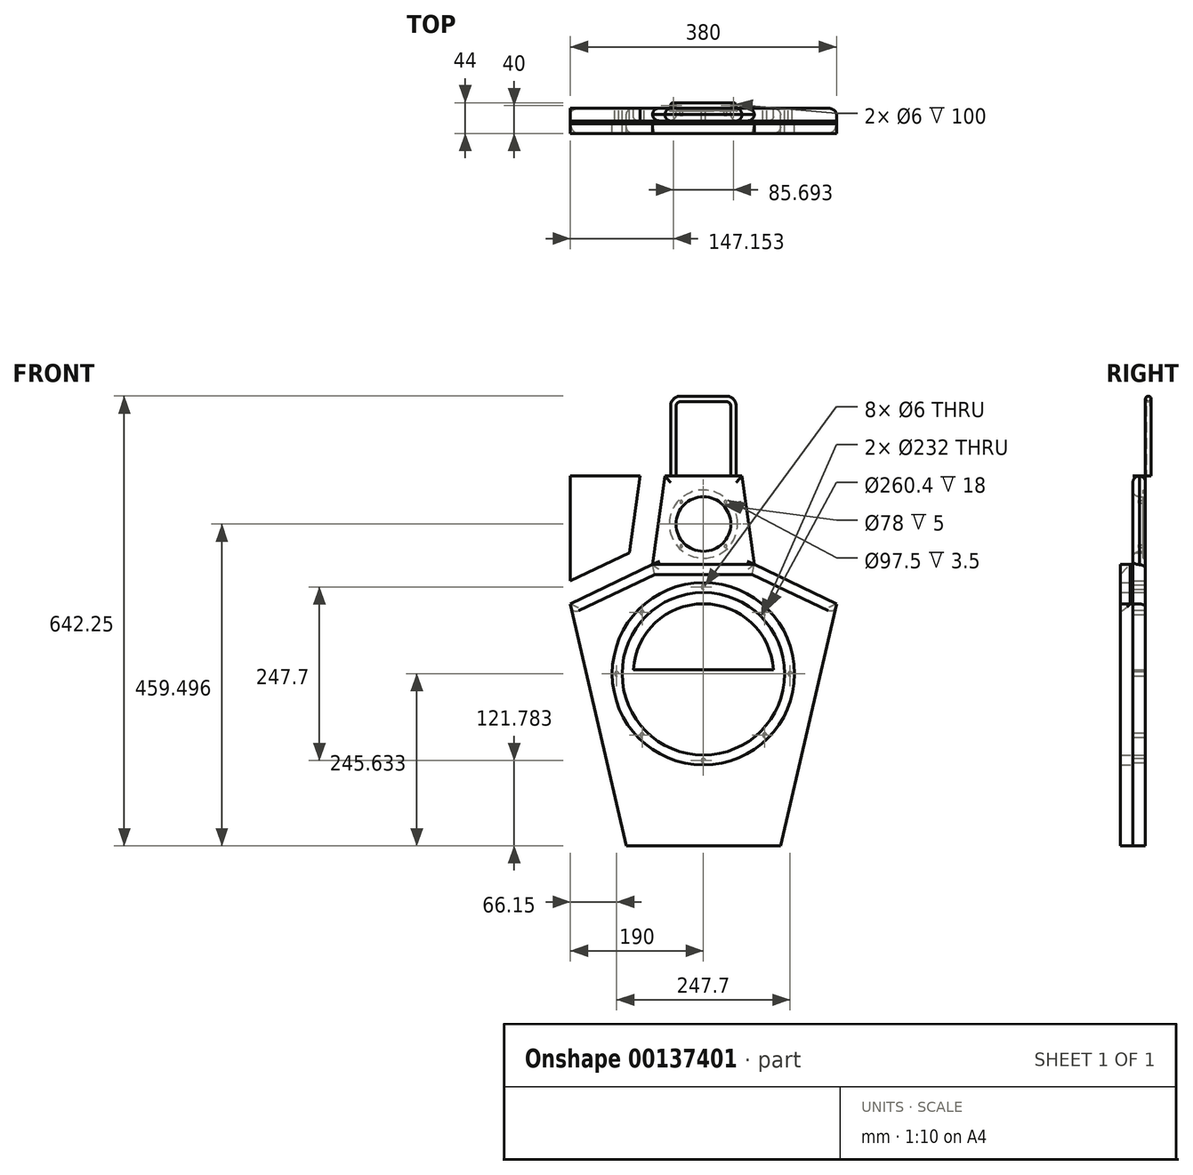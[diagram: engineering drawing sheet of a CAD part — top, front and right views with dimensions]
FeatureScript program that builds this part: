
annotation { "Feature Type Name" : "Feature", "Feature Type Description" : "" }
export const myFeature = defineFeature(function(context is Context, id is Id, definition is map)
    precondition{}
    {
        {
            var Q0;
            Q0=qCreatedBy(makeId("Front.planeOp"),FACE);
            var sketch = newSketch(context, id + "F0", { "sketchPlane" : qUnion([Q0])});
            skCircle(sketch, "E0", {"center": v(0, 113.89) * mm, "radius": 39 * mm});
            skCircle(sketch, "E1", {"center": v(0, -99.98) * mm, "radius": 116 * mm});
            skCircle(sketch, "E2", {"center": v(0, 113.89) * mm, "radius": 48.75 * mm, "construction": true});
            skCircle(sketch, "E3", {"center": v(0, -99.98) * mm, "radius": 130.2 * mm, "construction": true});
            skLineSegment(sketch, "E4", {"start": v(0, 270.1) * mm, "end": v(0, -456.04) * mm, "construction": true});
            skLineSegment(sketch, "E5", {"start": v(0, 182.64) * mm, "end": v(-55, 182.64) * mm});
            skCircle(sketch, "E6", {"center": v(0, -99.98) * mm, "radius": 146 * mm, "construction": true});
            skCircle(sketch, "E7", {"center": v(0, 113.89) * mm, "radius": 64 * mm, "construction": true});
            skLineSegment(sketch, "E8", {"start": v(-55, 182.64) * mm, "end": v(-72.73, 55.98) * mm});
            skLineSegment(sketch, "E9", {"start": v(0, -345.6) * mm, "end": v(-110, -345.6) * mm});
            skLineSegment(sketch, "E10", {"start": v(-110, -345.6) * mm, "end": v(-190, 0) * mm});
            skLineSegment(sketch, "E11", {"start": v(-72.73, 55.98) * mm, "end": v(-190, 0) * mm});
            skLineSegment(sketch, "E12.MirrorCS", {"start": v(0, 182.64) * mm, "end": v(55, 182.64) * mm});
            skLineSegment(sketch, "E13.MirrorCS", {"start": v(55, 182.64) * mm, "end": v(72.73, 55.98) * mm});
            skLineSegment(sketch, "E14.MirrorCS", {"start": v(72.73, 55.98) * mm, "end": v(190, 0) * mm});
            skLineSegment(sketch, "E15.MirrorCS", {"start": v(110, -345.6) * mm, "end": v(190, 0) * mm});
            skLineSegment(sketch, "E16.MirrorCS", {"start": v(0, -345.6) * mm, "end": v(110, -345.6) * mm});
            skLineSegment(sketch, "E17.bottom", {"start": v(-110, -195.6) * mm, "end": v(-92, -195.6) * mm, "construction": true});
            skLineSegment(sketch, "E17.top", {"start": v(-110, -345.6) * mm, "end": v(-92, -345.6) * mm});
            skLineSegment(sketch, "E17.left", {"start": v(-110, -195.6) * mm, "end": v(-110, -345.6) * mm, "construction": true});
            skLineSegment(sketch, "E17.right", {"start": v(-92, -195.6) * mm, "end": v(-92, -345.6) * mm, "construction": true});
            skLineSegment(sketch, "E18.MirrorCS", {"start": v(92, -195.6) * mm, "end": v(92, -345.6) * mm, "construction": true});
            skLineSegment(sketch, "E19.MirrorCS", {"start": v(110, -195.6) * mm, "end": v(92, -195.6) * mm, "construction": true});
            skLineSegment(sketch, "E20.MirrorCS", {"start": v(110, -195.6) * mm, "end": v(110, -345.6) * mm, "construction": true});
            skLineSegment(sketch, "E21.MirrorCS", {"start": v(110, -345.6) * mm, "end": v(92, -345.6) * mm, "construction": true});
            skLineSegment(sketch, "E22", {"start": v(-140.08, -245.59) * mm, "end": v(-90.27, -193.8) * mm, "construction": true});
            skLineSegment(sketch, "E23", {"start": v(-72.73, 55.98) * mm, "end": v(72.73, 55.98) * mm});
            skLineSegment(sketch, "E24", {"start": v(-92, -327.6) * mm, "end": v(92, -327.6) * mm, "construction": true});
            skLineSegment(sketch, "E25", {"start": v(-190, 182.64) * mm, "end": v(-90.37, 182.64) * mm});
            skLineSegment(sketch, "E26", {"start": v(-90.37, 182.64) * mm, "end": v(-105.74, 72.86) * mm});
            skLineSegment(sketch, "E27", {"start": v(-190, 32.64) * mm, "end": v(-105.74, 72.86) * mm});
            skLineSegment(sketch, "E28", {"start": v(-190, 32.64) * mm, "end": v(-190, 182.64) * mm});
            skLineSegment(sketch, "E29", {"start": v(-190, 0) * mm, "end": v(-190, 32.64) * mm, "construction": true});
            skLineSegment(sketch, "E30", {"start": v(-90.37, 182.64) * mm, "end": v(-55, 182.64) * mm, "construction": true});
            skCircle(sketch, "E31", {"center": v(0, -99.98) * mm, "radius": 100 * mm, "construction": true});
            skLineSegment(sketch, "E32", {"start": v(-99.82, -93.98) * mm, "end": v(99.82, -93.98) * mm});
            skLineSegment(sketch, "E33", {"start": v(-99.82, -105.98) * mm, "end": v(99.82, -105.98) * mm, "construction": true});
            skLineSegment(sketch, "E34", {"start": v(-100, -99.98) * mm, "end": v(100, -99.98) * mm, "construction": true});
            skArc(sketch, "E35", {"start": v(-99.82, -93.98) * mm, "mid": v(0, 0.02) * mm, "end": v(99.82, -93.98) * mm});
            skLineSegment(sketch, "E36", {"start": v(0, -345.6) * mm, "end": v(0, -245.98) * mm, "construction": true});
            skCircle(sketch, "E37", {"center": v(0, 113.89) * mm, "radius": 44.75 * mm, "construction": true});
            skLineSegment(sketch, "E38", {"start": v(-84.86, 113.89) * mm, "end": v(97.18, 113.89) * mm, "construction": true});
            skSolve(sketch);
        }
        {
            var Q0;
            Q0=makeQuery(id+"F0.imprint","IMPRINT",FACE,{"disambiguationData":[TD([[makeQuery(id+"F0.imprint","IMPRINT",EDGE,{"derivedFrom":sQuery(id+"F0.wireOp",EDGE,"E0")}),-1.0]])]});
            var Q1;
            Q1=makeQuery(id+"F0.imprint","IMPRINT",FACE,{"disambiguationData":[TD([[makeQuery(id+"F0.imprint","IMPRINT",EDGE,{"derivedFrom":sQuery(id+"F0.wireOp",EDGE,"E1")}),-1.0]])]});
            var Q2;
            Q2=makeQuery(id+"F0.imprint","IMPRINT",FACE,{"disambiguationData":[TD([[makeQuery(id+"F0.imprint","IMPRINT",EDGE,{"derivedFrom":sQuery(id+"F0.wireOp",EDGE,"ec5cafb6-0821-4271-814e-014075e78ac90.MirrorCS")}),1.0]])]});
            var Q3;
            Q3=makeQuery(id+"F0.imprint","IMPRINT",FACE,{"disambiguationData":[TD([[makeQuery(id+"F0.imprint","IMPRINT",EDGE,{"derivedFrom":sQuery(id+"F0.wireOp",EDGE,"eULuaSkG-qzq6-M7m6-OuyN-eB9Shyhv74vP")}),-1.0]])]});
            var Q4;
            Q4=makeQuery(id+"F0.imprint","IMPRINT",FACE,{"disambiguationData":[TD([[makeQuery(id+"F0.imprint","IMPRINT",EDGE,{"derivedFrom":sQuery(id+"F0.wireOp",EDGE,"wTw06wgs-Vm1q-qTd6-eUog-KbhtCCmFDIgU")}),1.0]])]});
            var Q5;
            Q5=makeQuery(id+"F0.imprint","IMPRINT",FACE,{"disambiguationData":[TD([[makeQuery(id+"F0.imprint","IMPRINT",EDGE,{"derivedFrom":sQuery(id+"F0.wireOp",EDGE,"97328e8b-8490-4f0b-808f-8670b9d821d80.MirrorC")}),-1.0]])]});
            var Q6;
            {var subQ0=sQuery(id+"F0.wireOp",EDGE,"54e6497e-5cba-44bf-835f-aaa9bed86e8d0.MirrorC");var subQ1=sQuery(id+"F0.wireOp",EDGE,"67c14ce4-3d45-40ac-80a8-5606c36c91ac.0");var subQ2=makeQuery(id+"F0.imprint","INTERSECT",VERTEX,{"disambiguationData":[OD(0.0)],"derivedFrom":[subQ1,subQ0]});Q6=makeQuery(id+"F0.imprint","IMPRINT",FACE,{"disambiguationData":[TD([[makeQuery(id+"F0.imprint","IMPRINT",EDGE,{"disambiguationData":[TD([[subQ2,-1.0]])],"derivedFrom":subQ1}),1.0]])]});}
            var Q7;
            {var subQ0=sQuery(id+"F0.wireOp",EDGE,"SJXep4Ca-SblW-kjJo-KBgL-TVq6fpib3Pzp");var subQ1=sQuery(id+"F0.wireOp",EDGE,"3cbaf5a3-71d0-46ca-a7cf-13315173ab510.MirrorCS");var subQ2=makeQuery(id+"F0.imprint","INTERSECT",VERTEX,{"disambiguationData":[OD(0.0)],"derivedFrom":[subQ1,subQ0]});Q7=makeQuery(id+"F0.imprint","IMPRINT",FACE,{"disambiguationData":[TD([[makeQuery(id+"F0.imprint","IMPRINT",EDGE,{"disambiguationData":[TD([[subQ2,-1.0]])],"derivedFrom":subQ1}),-1.0]])]});}
            extrude(context, id + "F1", {"entities" : qUnion([Q0, Q1, Q2, Q3, Q4, Q5, Q6, Q7]), "depth" : 18 * mm});
        }
        {
            var Q0;
            Q0=makeQuery(id+"F0.imprint","IMPRINT",FACE,{"disambiguationData":[TD([[makeQuery(id+"F0.imprint","IMPRINT",EDGE,{"derivedFrom":sQuery(id+"F0.wireOp",EDGE,"E1")}),-1.0]])]});
            var Q1;
            Q1=makeQuery(id+"F0.imprint","IMPRINT",FACE,{"disambiguationData":[TD([[makeQuery(id+"F0.imprint","IMPRINT",EDGE,{"derivedFrom":sQuery(id+"F0.wireOp",EDGE,"eULuaSkG-qzq6-M7m6-OuyN-eB9Shyhv74vP")}),-1.0]])]});
            var Q2;
            Q2=makeQuery(id+"F0.imprint","IMPRINT",FACE,{"disambiguationData":[TD([[makeQuery(id+"F0.imprint","IMPRINT",EDGE,{"derivedFrom":sQuery(id+"F0.wireOp",EDGE,"ec5cafb6-0821-4271-814e-014075e78ac90.MirrorCS")}),1.0]])]});
            var Q3;
            Q3=makeQuery(id+"F0.imprint","IMPRINT",FACE,{"disambiguationData":[TD([[makeQuery(id+"F0.imprint","IMPRINT",EDGE,{"derivedFrom":sQuery(id+"F0.wireOp",EDGE,"wTw06wgs-Vm1q-qTd6-eUog-KbhtCCmFDIgU")}),1.0]])]});
            var Q4;
            Q4=makeQuery(id+"F0.imprint","IMPRINT",FACE,{"disambiguationData":[TD([[makeQuery(id+"F0.imprint","IMPRINT",EDGE,{"derivedFrom":sQuery(id+"F0.wireOp",EDGE,"97328e8b-8490-4f0b-808f-8670b9d821d80.MirrorC")}),-1.0]])]});
            var Q5;
            {var subQ0=sQuery(id+"F0.wireOp",EDGE,"SJXep4Ca-SblW-kjJo-KBgL-TVq6fpib3Pzp");var subQ1=sQuery(id+"F0.wireOp",EDGE,"3cbaf5a3-71d0-46ca-a7cf-13315173ab510.MirrorCS");var subQ2=makeQuery(id+"F0.imprint","INTERSECT",VERTEX,{"disambiguationData":[OD(0.0)],"derivedFrom":[subQ1,subQ0]});Q5=makeQuery(id+"F0.imprint","IMPRINT",FACE,{"disambiguationData":[TD([[makeQuery(id+"F0.imprint","IMPRINT",EDGE,{"disambiguationData":[TD([[subQ2,-1.0]])],"derivedFrom":subQ1}),-1.0]])]});}
            var Q6;
            {var subQ0=sQuery(id+"F0.wireOp",EDGE,"54e6497e-5cba-44bf-835f-aaa9bed86e8d0.MirrorC");var subQ1=sQuery(id+"F0.wireOp",EDGE,"67c14ce4-3d45-40ac-80a8-5606c36c91ac.0");var subQ2=makeQuery(id+"F0.imprint","INTERSECT",VERTEX,{"disambiguationData":[OD(0.0)],"derivedFrom":[subQ1,subQ0]});Q6=makeQuery(id+"F0.imprint","IMPRINT",FACE,{"disambiguationData":[TD([[makeQuery(id+"F0.imprint","IMPRINT",EDGE,{"disambiguationData":[TD([[subQ2,-1.0]])],"derivedFrom":subQ1}),1.0]])]});}
            extrude(context, id + "F2", {"entities" : qUnion([Q0, Q1, Q2, Q3, Q4, Q5, Q6]), "depth" : 18 * mm});
        }
        {
            var Q0;
            Q0=makeQuery(id+"F2.opExtrude","SWEPT_BODY",BODY,{"disambiguationData":[OSD([sQuery(id+"F0.wireOp",EDGE,"E1"),sQuery(id+"F0.wireOp",EDGE,"E9"),sQuery(id+"F0.wireOp",EDGE,"E10"),sQuery(id+"F0.wireOp",EDGE,"E11"),sQuery(id+"F0.wireOp",EDGE,"E14.MirrorCS"),sQuery(id+"F0.wireOp",EDGE,"E15.MirrorCS"),sQuery(id+"F0.wireOp",EDGE,"E16.MirrorCS"),sQuery(id+"F0.wireOp",EDGE,"E17.top"),sQuery(id+"F0.wireOp",EDGE,"E23")])]});
            var Q1;
            Q1=makeQuery(id+"F2.opExtrude","SWEPT_EDGE",EDGE,{"disambiguationData":[OSD([sQuery(id+"F0.wireOp",EDGE,"E14.MirrorCS"),sQuery(id+"F0.wireOp",EDGE,"E15.MirrorCS")])]});
            transform(context, id + "F3", {"entities" : qUnion([Q0]), "transformType" : TransformType.TRANSLATION_DISTANCE, "transformDirection" : qUnion([Q1]), "distance" : 18 * mm, "oppositeDirection" : true, "makeCopy" : false});
        }
        {
            var Q0;
            Q0=makeQuery(id+"F0.imprint","IMPRINT",FACE,{"disambiguationData":[TD([[makeQuery(id+"F0.imprint","IMPRINT",EDGE,{"derivedFrom":sQuery(id+"F0.wireOp",EDGE,"E32")}),1.0]])]});
            extrude(context, id + "F4", {"entities" : qUnion([Q0]), "depth" : 18 * mm});
        }
        {
            var Q0;
            Q0=makeQuery(id+"F0.imprint","IMPRINT",FACE,{"disambiguationData":[TD([[makeQuery(id+"F0.imprint","IMPRINT",EDGE,{"derivedFrom":sQuery(id+"F0.wireOp",EDGE,"E25")}),-1.0]])]});
            extrude(context, id + "F5", {"entities" : qUnion([Q0]), "depth" : 18 * mm});
        }
        {
            var Q0;
            Q0=makeQuery(id+"F1.opExtrude","SWEPT_FACE",FACE,{"disambiguationData":[OSD([sQuery(id+"F0.wireOp",EDGE,"E5"),sQuery(id+"F0.wireOp",EDGE,"E12.MirrorCS")])]});
            var sketch = newSketch(context, id + "F6", { "sketchPlane" : qUnion([Q0])});
            skLineSegment(sketch, "E39", {"start": v(-42.85, 4) * mm, "end": v(42.85, 4) * mm, "construction": true});
            skLineSegment(sketch, "E40", {"start": v(0, 0) * mm, "end": v(0, -18) * mm, "construction": true});
            skCircle(sketch, "E41", {"center": v(-42.85, 4) * mm, "radius": 4 * mm});
            skCircle(sketch, "E42", {"center": v(-42.85, 4) * mm, "radius": 3 * mm});
            skCircle(sketch, "E43.MirrorC", {"center": v(42.85, 4) * mm, "radius": 3 * mm});
            skCircle(sketch, "E44.MirrorC", {"center": v(42.85, 4) * mm, "radius": 4 * mm});
            skSolve(sketch);
        }
        {
            var Q0;
            Q0=qCreatedBy(makeId("Front.planeOp"),FACE);
            cPlane(context, id + "F7", {"entities" : qUnion([Q0]), "cplaneType" : CPlaneType.OFFSET, "offset" : 4 * mm, "oppositeDirection" : true, "width" : 150 * mm, "height" : 150 * mm});
        }
        {
            var Q0;
            Q0=qCreatedBy(id+"F7.planeOp",FACE);
            var sketch = newSketch(context, id + "F8", { "sketchPlane" : qUnion([Q0])});
            skLineSegment(sketch, "E45", {"start": v(0, 225.34) * mm, "end": v(0, 315.34) * mm, "construction": true});
            skLineSegment(sketch, "E46", {"start": v(42.85, 182.64) * mm, "end": v(42.85, 282.64) * mm});
            skLineSegment(sketch, "E47", {"start": v(32.85, 292.64) * mm, "end": v(-32.85, 292.64) * mm});
            skLineSegment(sketch, "E48", {"start": v(-42.85, 282.64) * mm, "end": v(-42.85, 182.64) * mm});
            skPoint(sketch, "E49.visualSharp", {"position": v(-42.85, 292.64) * mm});
            skArc(sketch, "E49.filletArc", {"start": v(-32.85, 292.64) * mm, "mid": v(-39.92, 289.7) * mm, "end": v(-42.85, 282.64) * mm});
            skPoint(sketch, "E50.visualSharp", {"position": v(42.85, 292.64) * mm});
            skArc(sketch, "E50.filletArc", {"start": v(42.85, 282.64) * mm, "mid": v(39.92, 289.7) * mm, "end": v(32.85, 292.64) * mm});
            skSolve(sketch);
        }
        {
            var Q0;
            Q0=makeQuery(id+"F6.imprint","IMPRINT",FACE,{"disambiguationData":[TD([[makeQuery(id+"F6.imprint","IMPRINT",EDGE,{"derivedFrom":sQuery(id+"F6.wireOp",EDGE,"E41")}),1.0]])]});
            var Q1;
            Q1=sQuery(id+"F8.wireOp",EDGE,"E48");
            var Q2;
            Q2=sQuery(id+"F8.wireOp",EDGE,"E49.filletArc");
            var Q3;
            Q3=sQuery(id+"F8.wireOp",EDGE,"E47");
            var Q4;
            Q4=sQuery(id+"F8.wireOp",EDGE,"E50.filletArc");
            var Q5;
            Q5=sQuery(id+"F8.wireOp",EDGE,"E46");
            sweep(context, id + "F9", {"profiles" : qUnion([Q0]), "path" : qUnion([Q1, Q2, Q3, Q4, Q5])});
        }
        {
            var Q0;
            Q0=makeQuery(id+"F1.opExtrude","CAP_FACE",FACE,{"disambiguationData":[OSD([sQuery(id+"F0.wireOp",EDGE,"E0"),sQuery(id+"F0.wireOp",EDGE,"E1"),sQuery(id+"F0.wireOp",EDGE,"E5"),sQuery(id+"F0.wireOp",EDGE,"E8"),sQuery(id+"F0.wireOp",EDGE,"E9"),sQuery(id+"F0.wireOp",EDGE,"E10"),sQuery(id+"F0.wireOp",EDGE,"E11"),sQuery(id+"F0.wireOp",EDGE,"E12.MirrorCS"),sQuery(id+"F0.wireOp",EDGE,"E13.MirrorCS"),sQuery(id+"F0.wireOp",EDGE,"E14.MirrorCS"),sQuery(id+"F0.wireOp",EDGE,"E15.MirrorCS"),sQuery(id+"F0.wireOp",EDGE,"E16.MirrorCS"),sQuery(id+"F0.wireOp",EDGE,"E17.top")])],"isStart":false});
            var sketch = newSketch(context, id + "F10", { "sketchPlane" : qUnion([Q0])});
            skLineSegment(sketch, "E51.0", {"start": v(72.73, 55.98) * mm, "end": v(190, 0) * mm});
            skLineSegment(sketch, "E52.0", {"start": v(-72.73, 55.98) * mm, "end": v(72.73, 55.98) * mm});
            skLineSegment(sketch, "E53.0", {"start": v(-72.73, 55.98) * mm, "end": v(-190, 0) * mm});
            skLineSegment(sketch, "E54.0", {"start": v(110, -345.6) * mm, "end": v(190, 0) * mm});
            skLineSegment(sketch, "E55.0", {"start": v(-110, -345.6) * mm, "end": v(-190, 0) * mm});
            skLineSegment(sketch, "E56.0", {"start": v(0, -345.6) * mm, "end": v(110, -345.6) * mm});
            skLineSegment(sketch, "E57.0", {"start": v(0, -345.6) * mm, "end": v(-110, -345.6) * mm});
            skCircle(sketch, "E58.0", {"center": v(0, -99.98) * mm, "radius": 130.2 * mm});
            skSolve(sketch);
        }
        {
            var Q0;
            Q0=makeQuery(id+"F10.imprint","IMPRINT",FACE,{"disambiguationData":[TD([[makeQuery(id+"F10.imprint","IMPRINT",EDGE,{"derivedFrom":sQuery(id+"F10.wireOp",EDGE,"E51.0")}),-1.0]])]});
            extrude(context, id + "F11", {"entities" : qUnion([Q0]), "depth" : 18 * mm});
        }
        {
            var Q0;
            Q0=makeQuery(id+"F11.opExtrude","CAP_EDGE",EDGE,{"disambiguationData":[OSD([sQuery(id+"F10.wireOp",EDGE,"E52.0")])],"isStart":false});
            var Q1;
            Q1=makeQuery(id+"F11.opExtrude","CAP_EDGE",EDGE,{"disambiguationData":[OSD([sQuery(id+"F10.wireOp",EDGE,"E53.0")])],"isStart":false});
            var Q2;
            Q2=makeQuery(id+"F11.opExtrude","CAP_EDGE",EDGE,{"disambiguationData":[OSD([sQuery(id+"F10.wireOp",EDGE,"E51.0")])],"isStart":false});
            chamfer(context, id + "F12", {"entities" : qUnion([Q0, Q1, Q2]), "width" : 14 * mm, "tangentPropagation" : true});
        }
        {
            var Q0;
            Q0=makeQuery(id+"F11.opExtrude","CAP_EDGE",EDGE,{"disambiguationData":[OSD([sQuery(id+"F10.wireOp",EDGE,"E54.0")])],"isStart":false});
            var Q1;
            Q1=makeQuery(id+"F11.opExtrude","CAP_EDGE",EDGE,{"disambiguationData":[OSD([sQuery(id+"F10.wireOp",EDGE,"E55.0")])],"isStart":false});
            fillet(context, id + "F13", {"entities" : qUnion([Q0, Q1]), "radius" : 9.5 * mm, "tangentPropagation" : true, "allowEdgeOverflow" : false});
        }
        {
            var Q0;
            Q0=makeQuery(id+"F1.opExtrude","CAP_EDGE",EDGE,{"disambiguationData":[OSD([sQuery(id+"F0.wireOp",EDGE,"E8")])],"isStart":false});
            var Q1;
            Q1=makeQuery(id+"F1.opExtrude","CAP_EDGE",EDGE,{"disambiguationData":[OSD([sQuery(id+"F0.wireOp",EDGE,"E13.MirrorCS")])],"isStart":false});
            var Q2;
            Q2=makeQuery(id+"F1.opExtrude","CAP_EDGE",EDGE,{"disambiguationData":[OSD([sQuery(id+"F0.wireOp",EDGE,"E5"),sQuery(id+"F0.wireOp",EDGE,"E12.MirrorCS")])],"isStart":false});
            fillet(context, id + "F14", {"entities" : qUnion([Q0, Q1, Q2]), "radius" : 9.5 * mm, "tangentPropagation" : true, "allowEdgeOverflow" : false});
        }
        {
            var Q0;
            Q0=makeQuery(id+"F1.opExtrude","CAP_EDGE",EDGE,{"disambiguationData":[OSD([sQuery(id+"F0.wireOp",EDGE,"E5"),sQuery(id+"F0.wireOp",EDGE,"E12.MirrorCS")])],"isStart":true});
            var Q1;
            Q1=makeQuery(id+"F1.opExtrude","CAP_EDGE",EDGE,{"disambiguationData":[OSD([sQuery(id+"F0.wireOp",EDGE,"E8")])],"isStart":true});
            var Q2;
            Q2=makeQuery(id+"F1.opExtrude","CAP_EDGE",EDGE,{"disambiguationData":[OSD([sQuery(id+"F0.wireOp",EDGE,"E11")])],"isStart":true});
            var Q3;
            Q3=makeQuery(id+"F1.opExtrude","CAP_EDGE",EDGE,{"disambiguationData":[OSD([sQuery(id+"F0.wireOp",EDGE,"E10")])],"isStart":true});
            var Q4;
            Q4=makeQuery(id+"F1.opExtrude","CAP_EDGE",EDGE,{"disambiguationData":[OSD([sQuery(id+"F0.wireOp",EDGE,"E13.MirrorCS")])],"isStart":true});
            var Q5;
            Q5=makeQuery(id+"F1.opExtrude","CAP_EDGE",EDGE,{"disambiguationData":[OSD([sQuery(id+"F0.wireOp",EDGE,"E14.MirrorCS")])],"isStart":true});
            var Q6;
            Q6=makeQuery(id+"F1.opExtrude","CAP_EDGE",EDGE,{"disambiguationData":[OSD([sQuery(id+"F0.wireOp",EDGE,"E15.MirrorCS")])],"isStart":true});
            fillet(context, id + "F15", {"entities" : qUnion([Q0, Q1, Q2, Q3, Q4, Q5, Q6]), "radius" : 9.5 * mm, "tangentPropagation" : true, "allowEdgeOverflow" : false});
        }
        {
            var Q0;
            Q0=qCreatedBy(makeId("Front.planeOp"),FACE);
            var sketch = newSketch(context, id + "F16", { "sketchPlane" : qUnion([Q0])});
            skCircle(sketch, "E59.0", {"center": v(0, 113.89) * mm, "radius": 39 * mm});
            skCircle(sketch, "E60.0", {"center": v(0, 113.89) * mm, "radius": 48.75 * mm});
            skCircle(sketch, "E61", {"center": v(0, 113.89) * mm, "radius": 44.75 * mm, "construction": true});
            skCircle(sketch, "E62", {"center": v(44.75, 113.89) * mm, "radius": 1.9 * mm});
            skLineSegment(sketch, "E63", {"start": v(44.75, 113.89) * mm, "end": v(0, 113.89) * mm, "construction": true});
            skCircle(sketch, "E64.1.0", {"center": v(0, 158.64) * mm, "radius": 1.9 * mm});
            skCircle(sketch, "E64.2.0", {"center": v(-44.75, 113.89) * mm, "radius": 1.9 * mm});
            skCircle(sketch, "E64.3.0", {"center": v(0, 69.14) * mm, "radius": 1.9 * mm});
            skCircle(sketch, "E65.0", {"center": v(0, -99.98) * mm, "radius": 123.85 * mm, "construction": true});
            skCircle(sketch, "E66", {"center": v(123.85, -99.98) * mm, "radius": 3 * mm});
            skCircle(sketch, "E67.1.0", {"center": v(87.58, -12.4) * mm, "radius": 3 * mm});
            skCircle(sketch, "E67.2.0", {"center": v(0, 23.87) * mm, "radius": 3 * mm});
            skCircle(sketch, "E67.3.0", {"center": v(-87.58, -12.4) * mm, "radius": 3 * mm});
            skCircle(sketch, "E67.4.0", {"center": v(-123.85, -99.98) * mm, "radius": 3 * mm});
            skCircle(sketch, "E67.5.0", {"center": v(-87.58, -187.55) * mm, "radius": 3 * mm});
            skCircle(sketch, "E67.6.0", {"center": v(0, -223.83) * mm, "radius": 3 * mm});
            skCircle(sketch, "E67.7.0", {"center": v(87.58, -187.55) * mm, "radius": 3 * mm});
            skSolve(sketch);
        }
        {
            var Q0;
            Q0=makeQuery(id+"F16.imprint","IMPRINT",FACE,{"disambiguationData":[TD([[makeQuery(id+"F16.imprint","IMPRINT",EDGE,{"derivedFrom":sQuery(id+"F16.wireOp",EDGE,"E66")}),1.0]])]});
            var Q1;
            Q1=makeQuery(id+"F16.imprint","IMPRINT",FACE,{"disambiguationData":[TD([[makeQuery(id+"F16.imprint","IMPRINT",EDGE,{"derivedFrom":sQuery(id+"F16.wireOp",EDGE,"E67.1.0")}),1.0]])]});
            var Q2;
            Q2=makeQuery(id+"F16.imprint","IMPRINT",FACE,{"disambiguationData":[TD([[makeQuery(id+"F16.imprint","IMPRINT",EDGE,{"derivedFrom":sQuery(id+"F16.wireOp",EDGE,"E67.2.0")}),1.0]])]});
            var Q3;
            Q3=makeQuery(id+"F16.imprint","IMPRINT",FACE,{"disambiguationData":[TD([[makeQuery(id+"F16.imprint","IMPRINT",EDGE,{"derivedFrom":sQuery(id+"F16.wireOp",EDGE,"E67.3.0")}),1.0]])]});
            var Q4;
            Q4=makeQuery(id+"F16.imprint","IMPRINT",FACE,{"disambiguationData":[TD([[makeQuery(id+"F16.imprint","IMPRINT",EDGE,{"derivedFrom":sQuery(id+"F16.wireOp",EDGE,"E67.4.0")}),1.0]])]});
            var Q5;
            Q5=makeQuery(id+"F16.imprint","IMPRINT",FACE,{"disambiguationData":[TD([[makeQuery(id+"F16.imprint","IMPRINT",EDGE,{"derivedFrom":sQuery(id+"F16.wireOp",EDGE,"E67.5.0")}),1.0]])]});
            var Q6;
            Q6=makeQuery(id+"F16.imprint","IMPRINT",FACE,{"disambiguationData":[TD([[makeQuery(id+"F16.imprint","IMPRINT",EDGE,{"derivedFrom":sQuery(id+"F16.wireOp",EDGE,"E67.6.0")}),1.0]])]});
            var Q7;
            Q7=makeQuery(id+"F16.imprint","IMPRINT",FACE,{"disambiguationData":[TD([[makeQuery(id+"F16.imprint","IMPRINT",EDGE,{"derivedFrom":sQuery(id+"F16.wireOp",EDGE,"E67.7.0")}),1.0]])]});
            var Q8;
            Q8=makeQuery(id+"F1.opExtrude","CAP_FACE",FACE,{"disambiguationData":[OSD([sQuery(id+"F0.wireOp",EDGE,"E0"),sQuery(id+"F0.wireOp",EDGE,"E1"),sQuery(id+"F0.wireOp",EDGE,"E5"),sQuery(id+"F0.wireOp",EDGE,"E8"),sQuery(id+"F0.wireOp",EDGE,"E9"),sQuery(id+"F0.wireOp",EDGE,"E10"),sQuery(id+"F0.wireOp",EDGE,"E11"),sQuery(id+"F0.wireOp",EDGE,"E12.MirrorCS"),sQuery(id+"F0.wireOp",EDGE,"E13.MirrorCS"),sQuery(id+"F0.wireOp",EDGE,"E14.MirrorCS"),sQuery(id+"F0.wireOp",EDGE,"E15.MirrorCS"),sQuery(id+"F0.wireOp",EDGE,"E16.MirrorCS"),sQuery(id+"F0.wireOp",EDGE,"E17.top")])],"isStart":false});
            extrude(context, id + "F17", {"entities" : qUnion([Q0, Q1, Q2, Q3, Q4, Q5, Q6, Q7]), "operationType" : NewBodyOperationType.REMOVE, "endBound" : BoundingType.UP_TO_SURFACE, "endBoundEntityFace" : qUnion([Q8]), "depth" : 25 * mm});
        }
        {
            var Q0;
            Q0=makeQuery(id+"F0.imprint","IMPRINT",FACE,{"disambiguationData":[TD([[makeQuery(id+"F0.imprint","IMPRINT",EDGE,{"derivedFrom":sQuery(id+"F0.wireOp",EDGE,"E0")}),-1.0]])]});
            var sketch = newSketch(context, id + "F18", { "sketchPlane" : qUnion([Q0])});
            skCircle(sketch, "E68.0", {"center": v(0, 113.89) * mm, "radius": 39 * mm});
            skCircle(sketch, "E69.0", {"center": v(0, 113.89) * mm, "radius": 48.75 * mm});
            skSolve(sketch);
        }
        {
            var Q0;
            Q0=makeQuery(id+"F18.imprint","IMPRINT",FACE,{"disambiguationData":[TD([[makeQuery(id+"F18.imprint","IMPRINT",EDGE,{"derivedFrom":sQuery(id+"F18.wireOp",EDGE,"E68.0")}),-1.0]])]});
            extrude(context, id + "F19", {"entities" : qUnion([Q0]), "operationType" : NewBodyOperationType.REMOVE, "depth" : 3.5 * mm});
        }
        {
            var Q0;
            Q0=makeQuery(id+"F0.imprint","IMPRINT",FACE,{"disambiguationData":[TD([[makeQuery(id+"F0.imprint","IMPRINT",EDGE,{"derivedFrom":sQuery(id+"F0.wireOp",EDGE,"E0")}),-1.0]])]});
            var sketch = newSketch(context, id + "F20", { "sketchPlane" : qUnion([Q0])});
            skCircle(sketch, "E70.0", {"center": v(0, 113.89) * mm, "radius": 44.75 * mm, "construction": true});
            skCircle(sketch, "E71", {"center": v(31.64, 82.24) * mm, "radius": 1.9 * mm});
            skLineSegment(sketch, "E72", {"start": v(31.64, 82.24) * mm, "end": v(0, 113.89) * mm, "construction": true});
            skCircle(sketch, "E73.1.0", {"center": v(31.64, 145.53) * mm, "radius": 1.9 * mm});
            skCircle(sketch, "E73.2.0", {"center": v(-31.64, 145.53) * mm, "radius": 1.9 * mm});
            skCircle(sketch, "E73.3.0", {"center": v(-31.64, 82.24) * mm, "radius": 1.9 * mm});
            skSolve(sketch);
        }
        {
            var Q0;
            Q0=makeQuery(id+"F20.imprint","IMPRINT",FACE,{"disambiguationData":[TD([[makeQuery(id+"F20.imprint","IMPRINT",EDGE,{"derivedFrom":sQuery(id+"F20.wireOp",EDGE,"E71")}),1.0]])]});
            var Q1;
            Q1=makeQuery(id+"F20.imprint","IMPRINT",FACE,{"disambiguationData":[TD([[makeQuery(id+"F20.imprint","IMPRINT",EDGE,{"derivedFrom":sQuery(id+"F20.wireOp",EDGE,"E73.3.0")}),1.0]])]});
            var Q2;
            Q2=makeQuery(id+"F20.imprint","IMPRINT",FACE,{"disambiguationData":[TD([[makeQuery(id+"F20.imprint","IMPRINT",EDGE,{"derivedFrom":sQuery(id+"F20.wireOp",EDGE,"E73.2.0")}),1.0]])]});
            var Q3;
            Q3=makeQuery(id+"F20.imprint","IMPRINT",FACE,{"disambiguationData":[TD([[makeQuery(id+"F20.imprint","IMPRINT",EDGE,{"derivedFrom":sQuery(id+"F20.wireOp",EDGE,"E73.1.0")}),1.0]])]});
            extrude(context, id + "F21", {"entities" : qUnion([Q0, Q1, Q2, Q3]), "operationType" : NewBodyOperationType.REMOVE, "depth" : 10 * mm});
        }
        {
            var Q0;
            Q0=makeQuery(id+"F1.opExtrude","CAP_EDGE",EDGE,{"disambiguationData":[OSD([sQuery(id+"F0.wireOp",EDGE,"E0")])],"isStart":false});
            fillet(context, id + "F22", {"entities" : qUnion([Q0]), "radius" : 9.5 * mm, "tangentPropagation" : true, "allowEdgeOverflow" : false});
        }
        {
            var Q0;
            Q0=makeQuery(id+"F4.opExtrude","CAP_EDGE",EDGE,{"disambiguationData":[OSD([sQuery(id+"F0.wireOp",EDGE,"E35")])],"isStart":false});
            fillet(context, id + "F23", {"entities" : qUnion([Q0]), "radius" : 6.3 * mm, "tangentPropagation" : true, "allowEdgeOverflow" : false});
        }
    });
